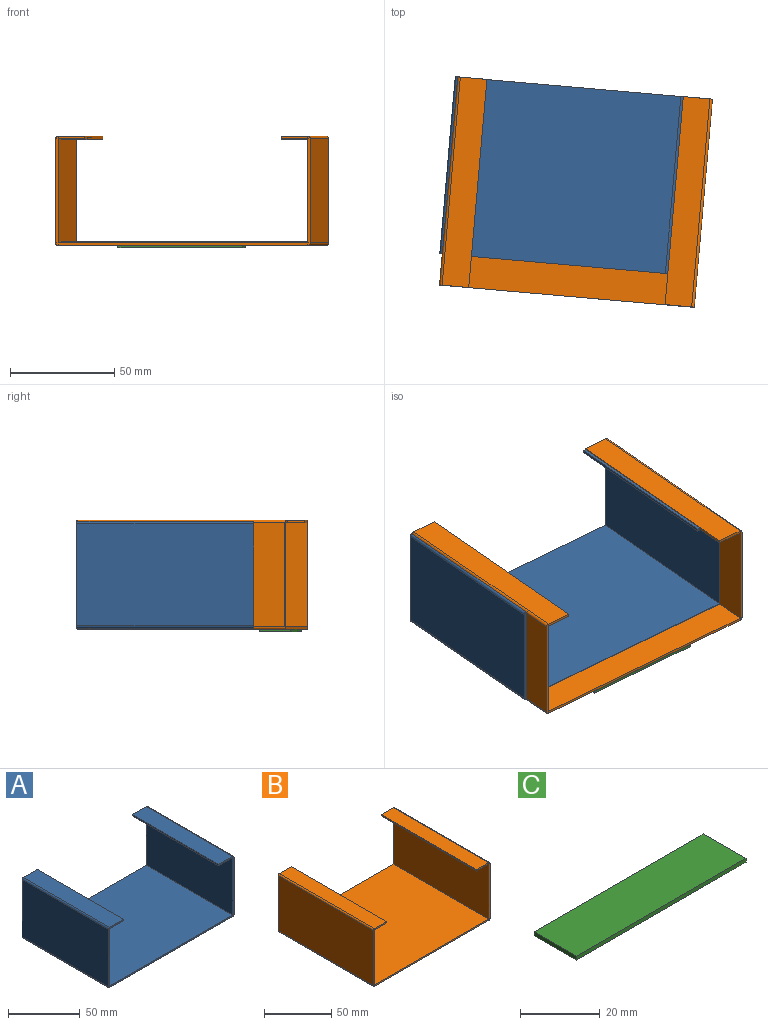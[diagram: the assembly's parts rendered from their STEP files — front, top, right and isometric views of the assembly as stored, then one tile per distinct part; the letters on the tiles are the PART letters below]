
ASSEMBLY  parts=3 mates=5
PART A: 38 faces, bbox 123.4x85x51.2 mm
  f0: plane 120.98x1.2mm, normal (0,1,0), area 145.2mm2, adj f2,f3,f18,f35
  f1: plane 120.98x1.2mm, normal (0,-1,0), area 145.2mm2, adj f2,f3,f17,f34
  f2: plane 120.98x85mm, normal (0,0,-1), area 10283.3mm2, adj f0,f1,f19,f36
  f3: plane 120.98x85mm, normal (0,0,1), area 10283.3mm2, adj f0,f1,f20,f37
  f4: plane 48.78x1.2mm, normal (0,1,0), area 58.5mm2, adj f6,f7,f14,f18
  f5: plane 48.78x1.2mm, normal (0,-1,0), area 58.5mm2, adj f6,f7,f13,f17
  f6: plane 85x48.78mm, normal (-1,0,0), area 4146.3mm2, adj f4,f5,f15,f19
  f7: plane 85x48.78mm, normal (1,0,0), area 4146.3mm2, adj f4,f5,f16,f20
  f8: plane 85x1.2mm, normal (1,0,0), area 102mm2, adj f9,f10,f11,f12
  f9: plane 13.79x1.2mm, normal (0,1,0), area 16.5mm2, adj f8,f11,f12,f14
  f10: plane 13.79x1.2mm, normal (0,-1,0), area 16.5mm2, adj f8,f11,f12,f13
  f11: plane 85x13.79mm, normal (0,0,1), area 1172.2mm2, adj f8,f9,f10,f15
  f12: plane 85x13.79mm, normal (0,0,-1), area 1172.2mm2, adj f8,f9,f10,f16
  f13: plane 1.21x1.21mm, normal (0,-1,0), area 1.1mm2, adj f5,f10,f15,f16
  f14: plane 1.21x1.21mm, normal (0,1,0), area 1.1mm2, adj f4,f9,f15,f16
  f15: cylinder r=1.21mm len=85mm, axis (0,-1,0), area 161.6mm2, adj f6,f11,f13,f14
  f16: cylinder r=0.01mm len=85mm, axis (0,-1,0), area 1.3mm2, adj f7,f12,f13,f14
  f17: plane 1.21x1.21mm, normal (0,-1,0), area 1.1mm2, adj f1,f5,f19,f20
  f18: plane 1.21x1.21mm, normal (0,1,0), area 1.1mm2, adj f0,f4,f19,f20
  f19: cylinder r=1.21mm len=85mm, axis (0,-1,0), area 161.6mm2, adj f2,f6,f17,f18
  f20: cylinder r=0.01mm len=85mm, axis (0,-1,0), area 1.3mm2, adj f3,f7,f17,f18
  f21: plane 48.78x1.2mm, normal (0,1,0), area 58.5mm2, adj f23,f24,f31,f35
  f22: plane 48.78x1.2mm, normal (0,-1,0), area 58.5mm2, adj f23,f24,f30,f34
  f23: plane 85x48.78mm, normal (1,0,0), area 4146.3mm2, adj f21,f22,f32,f36
  f24: plane 85x48.78mm, normal (-1,0,0), area 4146.3mm2, adj f21,f22,f33,f37
  f25: plane 85x1.2mm, normal (-1,0,0), area 102mm2, adj f26,f27,f28,f29
  f26: plane 13.79x1.2mm, normal (0,-1,0), area 16.5mm2, adj f25,f28,f29,f30
  f27: plane 13.79x1.2mm, normal (0,1,0), area 16.5mm2, adj f25,f28,f29,f31
  f28: plane 85x13.79mm, normal (0,0,1), area 1172.1mm2, adj f25,f26,f27,f32
  f29: plane 85x13.79mm, normal (0,0,-1), area 1172.1mm2, adj f25,f26,f27,f33
  f30: plane 1.21x1.21mm, normal (0,-1,0), area 1.1mm2, adj f22,f26,f32,f33
  f31: plane 1.21x1.21mm, normal (0,1,0), area 1.1mm2, adj f21,f27,f32,f33
  f32: cylinder r=1.21mm len=85mm, axis (0,-1,0), area 161.6mm2, adj f23,f28,f30,f31
  f33: cylinder r=0.01mm len=85mm, axis (0,-1,0), area 1.3mm2, adj f24,f29,f30,f31
  f34: plane 1.21x1.21mm, normal (0,-1,0), area 1.1mm2, adj f1,f22,f36,f37
  f35: plane 1.21x1.21mm, normal (0,1,0), area 1.1mm2, adj f0,f21,f36,f37
  f36: cylinder r=1.21mm len=85mm, axis (0,-1,0), area 161.6mm2, adj f2,f23,f34,f35
  f37: cylinder r=0.01mm len=85mm, axis (0,-1,0), area 1.3mm2, adj f3,f24,f34,f35
PART B: 38 faces, bbox 122.4x100x52.4 mm
  f0: plane 119.98x1.2mm, normal (0,1,0), area 144mm2, adj f2,f3,f18,f35
  f1: plane 119.98x1.2mm, normal (0,-1,0), area 144mm2, adj f2,f3,f17,f34
  f2: plane 119.98x100mm, normal (0,0,-1), area 11998mm2, adj f0,f1,f19,f36
  f3: plane 119.98x100mm, normal (0,0,1), area 11998mm2, adj f0,f1,f20,f37
  f4: plane 49.98x1.2mm, normal (0,1,0), area 60mm2, adj f6,f7,f14,f18
  f5: plane 49.98x1.2mm, normal (0,-1,0), area 60mm2, adj f6,f7,f13,f17
  f6: plane 100x49.98mm, normal (-1,0,0), area 4998mm2, adj f4,f5,f15,f19
  f7: plane 100x49.98mm, normal (1,0,0), area 4998mm2, adj f4,f5,f16,f20
  f8: plane 100x1.2mm, normal (1,0,0), area 120mm2, adj f9,f10,f11,f12
  f9: plane 12.79x1.2mm, normal (0,1,0), area 15.3mm2, adj f8,f11,f12,f14
  f10: plane 12.79x1.2mm, normal (0,-1,0), area 15.3mm2, adj f8,f11,f12,f13
  f11: plane 100x12.79mm, normal (0,0,1), area 1279mm2, adj f8,f9,f10,f15
  f12: plane 100x12.79mm, normal (0,0,-1), area 1279mm2, adj f8,f9,f10,f16
  f13: plane 1.21x1.21mm, normal (0,-1,0), area 1.1mm2, adj f5,f10,f15,f16
  f14: plane 1.21x1.21mm, normal (0,1,0), area 1.1mm2, adj f4,f9,f15,f16
  f15: cylinder r=1.21mm len=100mm, axis (0,-1,0), area 190.1mm2, adj f6,f11,f13,f14
  f16: cylinder r=0.01mm len=100mm, axis (0,-1,0), area 1.6mm2, adj f7,f12,f13,f14
  f17: plane 1.21x1.21mm, normal (0,-1,0), area 1.1mm2, adj f1,f5,f19,f20
  f18: plane 1.21x1.21mm, normal (0,1,0), area 1.1mm2, adj f0,f4,f19,f20
  f19: cylinder r=1.21mm len=100mm, axis (0,-1,0), area 190.1mm2, adj f2,f6,f17,f18
  f20: cylinder r=0.01mm len=100mm, axis (0,-1,0), area 1.6mm2, adj f3,f7,f17,f18
  f21: plane 49.98x1.2mm, normal (0,1,0), area 60mm2, adj f23,f24,f31,f35
  f22: plane 49.98x1.2mm, normal (0,-1,0), area 60mm2, adj f23,f24,f30,f34
  f23: plane 100x49.98mm, normal (1,0,0), area 4998mm2, adj f21,f22,f32,f36
  f24: plane 100x49.98mm, normal (-1,0,0), area 4998mm2, adj f21,f22,f33,f37
  f25: plane 100x1.2mm, normal (-1,0,0), area 120mm2, adj f26,f27,f28,f29
  f26: plane 12.79x1.2mm, normal (0,-1,0), area 15.3mm2, adj f25,f28,f29,f30
  f27: plane 12.79x1.2mm, normal (0,1,0), area 15.3mm2, adj f25,f28,f29,f31
  f28: plane 100x12.79mm, normal (0,0,1), area 1279mm2, adj f25,f26,f27,f32
  f29: plane 100x12.79mm, normal (0,0,-1), area 1279mm2, adj f25,f26,f27,f33
  f30: plane 1.21x1.21mm, normal (0,-1,0), area 1.1mm2, adj f22,f26,f32,f33
  f31: plane 1.21x1.21mm, normal (0,1,0), area 1.1mm2, adj f21,f27,f32,f33
  f32: cylinder r=1.21mm len=100mm, axis (0,-1,0), area 190.1mm2, adj f23,f28,f30,f31
  f33: cylinder r=0.01mm len=100mm, axis (0,-1,0), area 1.6mm2, adj f24,f29,f30,f31
  f34: plane 1.21x1.21mm, normal (0,-1,0), area 1.1mm2, adj f1,f22,f36,f37
  f35: plane 1.21x1.21mm, normal (0,1,0), area 1.1mm2, adj f0,f21,f36,f37
  f36: cylinder r=1.21mm len=100mm, axis (0,-1,0), area 190.1mm2, adj f2,f23,f34,f35
  f37: cylinder r=0.01mm len=100mm, axis (0,-1,0), area 1.6mm2, adj f3,f24,f34,f35
PART C: 6 faces, bbox 60x15x1.2 mm
  f0: plane 60x1.2mm, normal (0,1,0), area 72mm2, adj f1,f3,f4,f5
  f1: plane 15x1.2mm, normal (1,0,0), area 18mm2, adj f0,f2,f4,f5
  f2: plane 60x1.2mm, normal (0,-1,0), area 72mm2, adj f1,f3,f4,f5
  f3: plane 15x1.2mm, normal (-1,0,0), area 18mm2, adj f0,f2,f4,f5
  f4: plane 60x15mm, normal (0,0,-1), area 900mm2, adj f0,f1,f2,f3
  f5: plane 60x15mm, normal (0,0,1), area 900mm2, adj f0,f1,f2,f3
PLACE A rot(axis=(0,0,-1),5deg) t=(-33.13,-9.99,-1.64)mm
PLACE B rot(axis=(0,0,1),175deg) t=(96.21,64.02,-1.04)mm
PLACE C rot(axis=(0,0,-1),5deg) t=(-3.35,-27.65,-2.24)mm
MATE parallel A.f7 <-> B.f23  axis (1,-0.09,0) through (-31.93,-10.09,23.96)mm
MATE planar C.f2 <-> B.f0  axis (-0.09,-1,0) through (26.53,-30.26,-2.84)mm
MATE planar B.f2 <-> C.f5  axis (0,0,-1) through (32.08,19.44,-2.24)mm
MATE parallel B.f23 <-> C.f3  axis (-1,0.09,0) through (-28.88,24.78,23.96)mm
MATE planar C.f0 <-> A.f1  axis (0.09,1,0) through (27.84,-15.32,-2.84)mm
